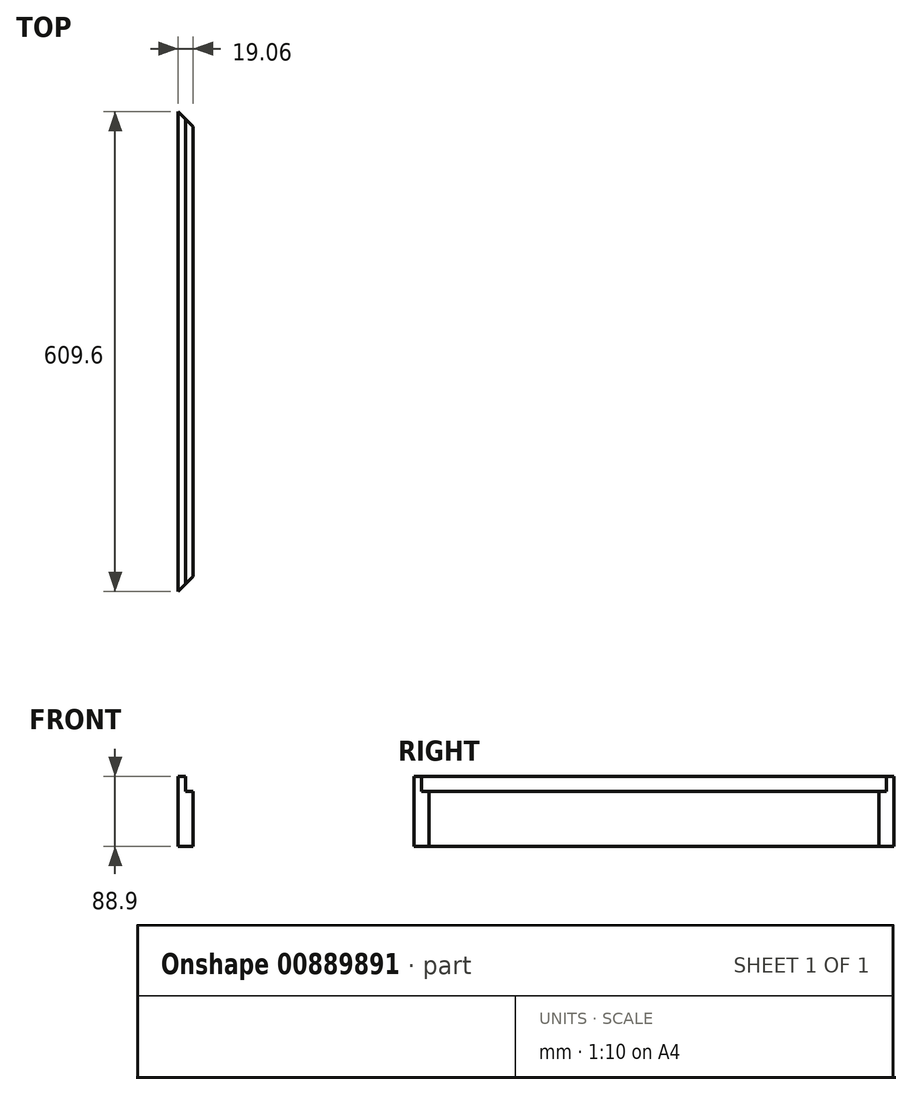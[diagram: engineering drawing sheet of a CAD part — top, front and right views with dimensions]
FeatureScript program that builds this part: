
annotation { "Feature Type Name" : "Feature", "Feature Type Description" : "" }
export const myFeature = defineFeature(function(context is Context, id is Id, definition is map)
    precondition{}
    {
        {
            var Q0;
            Q0=qCreatedBy(makeId("Front.planeOp"),FACE);
            var sketch = newSketch(context, id + "F0", { "sketchPlane" : qUnion([Q0])});
            skLineSegment(sketch, "E0.bottom", {"start": v(9.53, -44.45) * mm, "end": v(-9.52, -44.45) * mm});
            skLineSegment(sketch, "E0.top", {"start": v(9.53, 44.45) * mm, "end": v(-9.52, 44.45) * mm});
            skLineSegment(sketch, "E0.left", {"start": v(9.53, -44.45) * mm, "end": v(9.53, 44.45) * mm});
            skLineSegment(sketch, "E0.right", {"start": v(-9.52, -44.45) * mm, "end": v(-9.52, 44.45) * mm});
            skPoint(sketch, "E0.middle", {"position": v(0, 0) * mm});
            skSolve(sketch);
        }
        {
            var Q0;
            Q0 = qSketchRegion(id + "F0", true);
            extrude(context, id + "F1", {"entities" : qUnion([Q0]), "depth" : 609.6 * mm, "offsetDistance" : 25.4 * mm});
        }
        {
            var Q0;
            Q0=makeQuery(id+"F1.opExtrude","SWEPT_FACE",FACE,{"disambiguationData":[OSD([sQuery(id+"F0.wireOp",EDGE,"E0.top")])]});
            var sketch = newSketch(context, id + "F2", { "sketchPlane" : qUnion([Q0])});
            skLineSegment(sketch, "E1", {"start": v(-9.52, -609.6) * mm, "end": v(9.53, -609.6) * mm});
            skLineSegment(sketch, "E2", {"start": v(9.53, -609.6) * mm, "end": v(9.53, -590.55) * mm});
            skLineSegment(sketch, "E3", {"start": v(9.52, -590.55) * mm, "end": v(-9.53, -609.6) * mm});
            skLineSegment(sketch, "E4", {"start": v(-9.52, 0) * mm, "end": v(9.53, 0) * mm});
            skLineSegment(sketch, "E5", {"start": v(9.53, 0) * mm, "end": v(9.53, -19.05) * mm});
            skLineSegment(sketch, "E6", {"start": v(9.53, -19.05) * mm, "end": v(-9.52, 0) * mm});
            skSolve(sketch);
        }
        {
            var Q0;
            Q0 = qSketchRegion(id + "F2", true);
            extrude(context, id + "F3", {"entities" : qUnion([Q0]), "operationType" : NewBodyOperationType.REMOVE, "endBound" : BoundingType.THROUGH_ALL, "oppositeDirection" : true, "depth" : 25.4 * mm, "offsetDistance" : 25.4 * mm});
        }
        {
            var Q0;
            Q0=makeQuery(id+"F1.opExtrude","SWEPT_FACE",FACE,{"disambiguationData":[OSD([sQuery(id+"F0.wireOp",EDGE,"E0.top")])]});
            var sketch = newSketch(context, id + "F4", { "sketchPlane" : qUnion([Q0])});
            skLineSegment(sketch, "E7", {"start": v(0, -600.08) * mm, "end": v(0, -9.53) * mm});
            skLineSegment(sketch, "E8", {"start": v(0, -9.53) * mm, "end": v(9.53, -19.05) * mm});
            skLineSegment(sketch, "E9", {"start": v(9.53, -19.05) * mm, "end": v(9.53, -590.55) * mm});
            skLineSegment(sketch, "E10", {"start": v(9.53, -590.55) * mm, "end": v(0, -600.08) * mm});
            skSolve(sketch);
        }
        {
            var Q0;
            Q0=makeQuery(id+"F4.imprint","IMPRINT",FACE,{"disambiguationData":[TD([[makeQuery(id+"F4.imprint","IMPRINT",EDGE,{"derivedFrom":sQuery(id+"F4.wireOp",EDGE,"E7")}),-1.0]])]});
            extrude(context, id + "F5", {"entities" : qUnion([Q0]), "operationType" : NewBodyOperationType.REMOVE, "oppositeDirection" : true, "depth" : 19.05 * mm, "offsetDistance" : 25.4 * mm});
        }
    });
